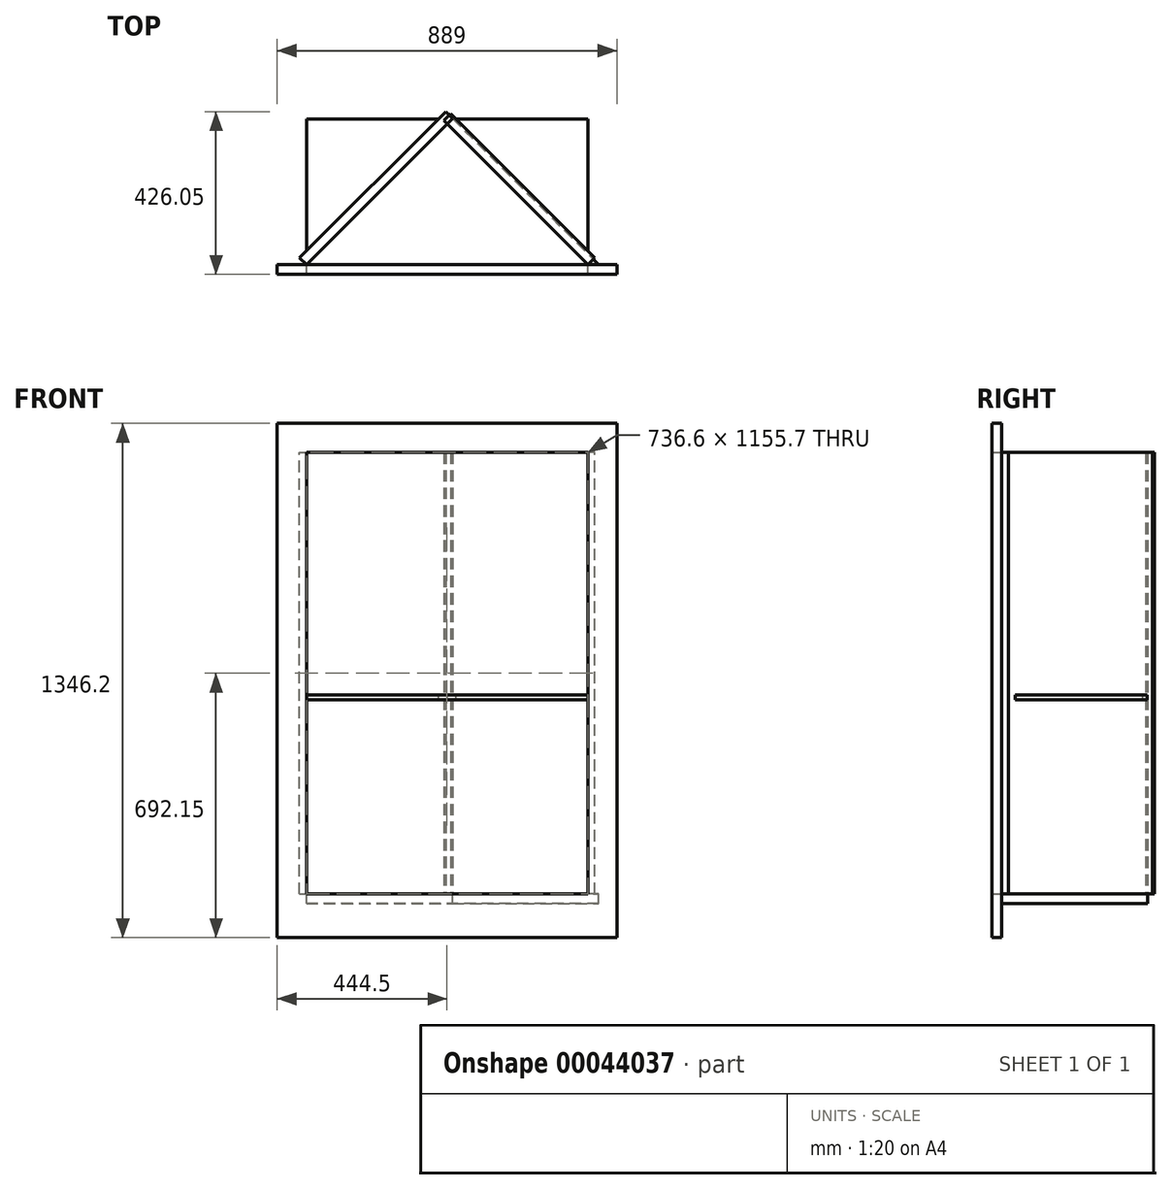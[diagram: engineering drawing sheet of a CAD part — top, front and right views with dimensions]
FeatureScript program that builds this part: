
annotation { "Feature Type Name" : "Feature", "Feature Type Description" : "" }
export const myFeature = defineFeature(function(context is Context, id is Id, definition is map)
    precondition{}
    {
        {
            var Q0;
            Q0=qCreatedBy(makeId("Front.planeOp"),FACE);
            var sketch = newSketch(context, id + "F0", { "sketchPlane" : qUnion([Q0])});
            skLineSegment(sketch, "E0.bottom", {"start": v(0, 0) * mm, "end": v(-889, 0) * mm});
            skLineSegment(sketch, "E0.top", {"start": v(0, 1346.2) * mm, "end": v(-889, 1346.2) * mm});
            skLineSegment(sketch, "E0.left", {"start": v(0, 0) * mm, "end": v(0, 1346.2) * mm});
            skLineSegment(sketch, "E0.right", {"start": v(-889, 0) * mm, "end": v(-889, 1346.2) * mm});
            skLineSegment(sketch, "E1.0", {"start": v(-76.2, 0) * mm, "end": v(-76.2, 1346.2) * mm});
            skLineSegment(sketch, "E2.0", {"start": v(0, 1270) * mm, "end": v(-889, 1270) * mm});
            skLineSegment(sketch, "E3.0", {"start": v(-812.8, 0) * mm, "end": v(-812.8, 1346.2) * mm});
            skLineSegment(sketch, "E4.0", {"start": v(0, 114.3) * mm, "end": v(-889, 114.3) * mm});
            skSolve(sketch);
        }
        {
            var Q0;
            Q0 = qSketchRegion(id + "F0", true);
            extrude(context, id + "F1", {"entities" : qUnion([Q0]), "depth" : 25.4 * mm});
        }
        {
            var Q0;
            Q0=qCreatedBy(makeId("Front.planeOp"),FACE);
            var sketch = newSketch(context, id + "F2", { "sketchPlane" : qUnion([Q0])});
            skLineSegment(sketch, "E5.0", {"start": v(-812.8, 114.3) * mm, "end": v(-812.8, 1270) * mm});
            skLineSegment(sketch, "E6.0", {"start": v(-76.2, 114.3) * mm, "end": v(-76.2, 1270) * mm});
            skLineSegment(sketch, "E7.bottom", {"start": v(-812.8, 635) * mm, "end": v(-76.2, 635) * mm});
            skLineSegment(sketch, "E7.top", {"start": v(-812.8, 622.3) * mm, "end": v(-76.2, 622.3) * mm});
            skLineSegment(sketch, "E7.left", {"start": v(-812.8, 635) * mm, "end": v(-812.8, 622.3) * mm});
            skLineSegment(sketch, "E7.right", {"start": v(-76.2, 635) * mm, "end": v(-76.2, 622.3) * mm});
            skSolve(sketch);
        }
        {
            var Q0;
            Q0 = qSketchRegion(id + "F2", true);
            extrude(context, id + "F3", {"entities" : qUnion([Q0]), "oppositeDirection" : true, "depth" : 381 * mm});
        }
        {
            var Q0;
            Q0=makeQuery(id+"F1.opExtrude","CAP_EDGE",EDGE,{"disambiguationData":[OSD([sQuery(id+"F0.wireOp",EDGE,"E1.0")])],"isStart":true});
            cPlane(context, id + "F4", {"entities" : qUnion([Q0]), "cplaneType" : CPlaneType.LINE_ANGLE, "offset" : 152.4 * mm, "angle" : 45 * degree, "width" : 152.4 * mm, "height" : 152.4 * mm});
        }
        {
            var Q0;
            Q0=qCreatedBy(id+"F4.planeOp",FACE);
            var sketch = newSketch(context, id + "F5", { "sketchPlane" : qUnion([Q0])});
            skLineSegment(sketch, "E8.0", {"start": v(53.88, 114.3) * mm, "end": v(53.88, 1270) * mm});
            skLineSegment(sketch, "E9.bottom", {"start": v(53.88, 1270) * mm, "end": v(587.28, 1270) * mm});
            skLineSegment(sketch, "E9.top", {"start": v(53.88, 114.3) * mm, "end": v(587.28, 114.3) * mm});
            skLineSegment(sketch, "E9.left", {"start": v(53.88, 1270) * mm, "end": v(53.88, 114.3) * mm});
            skLineSegment(sketch, "E9.right", {"start": v(587.28, 1270) * mm, "end": v(587.28, 114.3) * mm});
            skSolve(sketch);
        }
        {
            var Q0;
            Q0 = qSketchRegion(id + "F5", true);
            extrude(context, id + "F6", {"entities" : qUnion([Q0]), "depth" : 25.4 * mm});
        }
        {
            var Q0;
            Q0=makeQuery(id+"F1.opExtrude","CAP_EDGE",EDGE,{"disambiguationData":[OSD([sQuery(id+"F0.wireOp",EDGE,"E3.0")])],"isStart":true});
            cPlane(context, id + "F7", {"entities" : qUnion([Q0]), "cplaneType" : CPlaneType.LINE_ANGLE, "offset" : 152.4 * mm, "angle" : 135 * degree, "width" : 152.4 * mm, "height" : 152.4 * mm});
        }
        {
            var Q0;
            Q0=qCreatedBy(id+"F7.planeOp",FACE);
            var sketch = newSketch(context, id + "F8", { "sketchPlane" : qUnion([Q0])});
            skLineSegment(sketch, "E10.0", {"start": v(574.74, 114.3) * mm, "end": v(574.74, 1270) * mm});
            skLineSegment(sketch, "E11.bottom", {"start": v(574.74, 1270) * mm, "end": v(33.54, 1270) * mm});
            skLineSegment(sketch, "E11.top", {"start": v(574.74, 114.3) * mm, "end": v(33.54, 114.3) * mm});
            skLineSegment(sketch, "E11.left", {"start": v(574.74, 1270) * mm, "end": v(574.74, 114.3) * mm});
            skLineSegment(sketch, "E11.right", {"start": v(33.54, 1270) * mm, "end": v(33.54, 114.3) * mm});
            skSolve(sketch);
        }
        {
            var Q0;
            Q0 = qSketchRegion(id + "F8", true);
            extrude(context, id + "F9", {"entities" : qUnion([Q0]), "depth" : 25.4 * mm});
        }
        {
            var Q0;
            Q0=makeQuery(id+"F9.opExtrude","SWEPT_FACE",FACE,{"disambiguationData":[OSD([sQuery(id+"F8.wireOp",EDGE,"E11.top")])]});
            var sketch = newSketch(context, id + "F10", { "sketchPlane" : qUnion([Q0])});
            skLineSegment(sketch, "E12", {"start": v(-812.8, 0) * mm, "end": v(-430.12, -382.68) * mm});
            skLineSegment(sketch, "E13", {"start": v(-430.12, -382.68) * mm, "end": v(-47.43, 0) * mm});
            skLineSegment(sketch, "E14", {"start": v(-47.43, 0) * mm, "end": v(-812.8, 0) * mm});
            skSolve(sketch);
        }
        {
            var Q0;
            Q0 = qSketchRegion(id + "F10", true);
            extrude(context, id + "F11", {"entities" : qUnion([Q0]), "depth" : 25.4 * mm});
        }
        {
            var Q0;
            Q0=makeQuery(id+"F9.opExtrude","SWEPT_BODY",BODY,{"disambiguationData":[OSD([sQuery(id+"F8.wireOp",EDGE,"E11.bottom"),sQuery(id+"F8.wireOp",EDGE,"E11.top"),sQuery(id+"F8.wireOp",EDGE,"E11.left"),sQuery(id+"F8.wireOp",EDGE,"E11.right")])]});
            var Q1;
            Q1=makeQuery(id+"F6.opExtrude","SWEPT_BODY",BODY,{"disambiguationData":[OSD([sQuery(id+"F5.wireOp",EDGE,"E9.bottom"),sQuery(id+"F5.wireOp",EDGE,"E9.top"),sQuery(id+"F5.wireOp",EDGE,"E9.left"),sQuery(id+"F5.wireOp",EDGE,"E9.right")])]});
            var Q2;
            Q2=makeQuery(id+"F3.opExtrude","SWEPT_BODY",BODY,{"disambiguationData":[OSD([sQuery(id+"F2.wireOp",EDGE,"E7.bottom"),sQuery(id+"F2.wireOp",EDGE,"E7.top"),sQuery(id+"F2.wireOp",EDGE,"E7.left"),sQuery(id+"F2.wireOp",EDGE,"E7.right")])]});
            booleanBodies(context, id + "F12", {"operationType" : BooleanOperationType.SUBTRACTION, "tools" : qUnion([Q0, Q1]), "targets" : qUnion([Q2]), "keepTools" : true});
        }
    });
